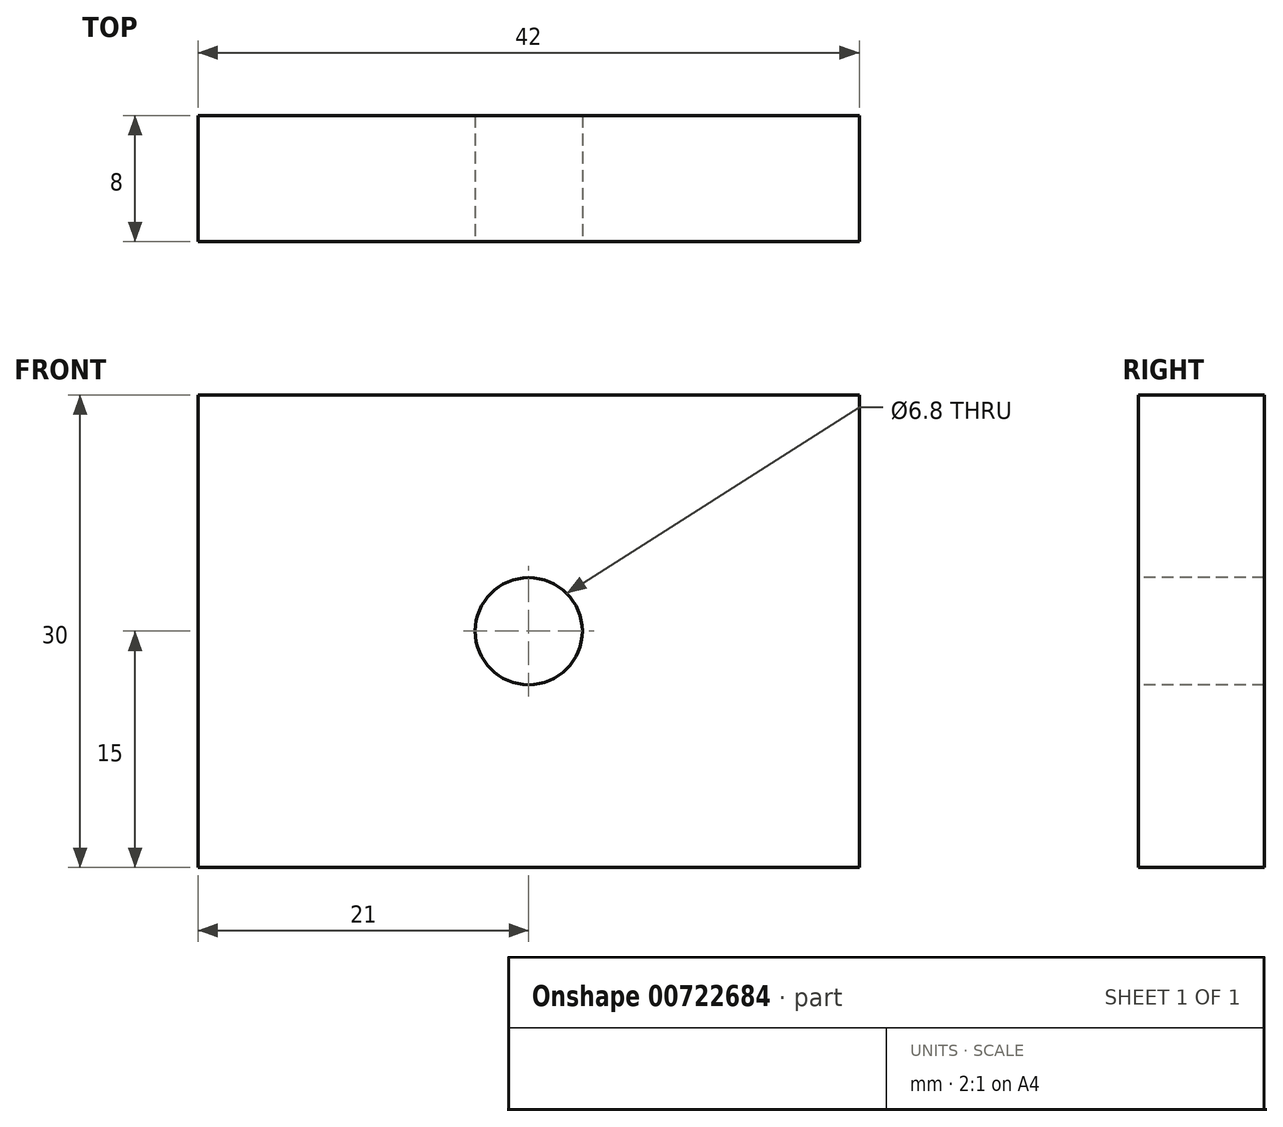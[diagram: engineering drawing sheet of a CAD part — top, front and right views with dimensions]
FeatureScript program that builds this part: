
annotation { "Feature Type Name" : "Feature", "Feature Type Description" : "" }
export const myFeature = defineFeature(function(context is Context, id is Id, definition is map)
    precondition{}
    {
        {
            var Q0;
            Q0=qCreatedBy(makeId("Front.planeOp"),FACE);
            var sketch = newSketch(context, id + "F0", { "sketchPlane" : qUnion([Q0])});
            skLineSegment(sketch, "E0.bottom", {"start": v(21, 15) * mm, "end": v(-21, 15) * mm});
            skLineSegment(sketch, "E0.top", {"start": v(21, -15) * mm, "end": v(-21, -15) * mm});
            skLineSegment(sketch, "E0.left", {"start": v(21, 15) * mm, "end": v(21, -15) * mm});
            skLineSegment(sketch, "E0.right", {"start": v(-21, 15) * mm, "end": v(-21, -15) * mm});
            skPoint(sketch, "E0.middle", {"position": v(0, 0) * mm});
            skSolve(sketch);
        }
        {
            var Q0;
            Q0 = qSketchRegion(id + "F0", true);
            extrude(context, id + "F1", {"entities" : qUnion([Q0]), "depth" : 8 * mm, "offsetDistance" : 25 * mm});
        }
        {
            var Q0;
            Q0=sQuery(id+"F0.wireOp",VERTEX,"E0.middle");
            var Q1;
            Q1=makeQuery(id+"F1.opExtrude","SWEPT_BODY",BODY,{"disambiguationData":[OSD([sQuery(id+"F0.wireOp",EDGE,"E0.bottom"),sQuery(id+"F0.wireOp",EDGE,"E0.top"),sQuery(id+"F0.wireOp",EDGE,"E0.left"),sQuery(id+"F0.wireOp",EDGE,"E0.right")])]});
            hole(context, id + "F2", {"style" : HoleStyle.SIMPLE, "endStyle" : HoleEndStyle.THROUGH, "oppositeDirection" : true, "holeDiameter" : 6.8 * mm, "majorDiameter" : 5 * mm, "isTappedThrough" : true, "tappedDepth" : 12 * mm, "tapClearance" : 3, "locations" : qUnion([Q0]), "scope" : qUnion([Q1])});
        }
    });
